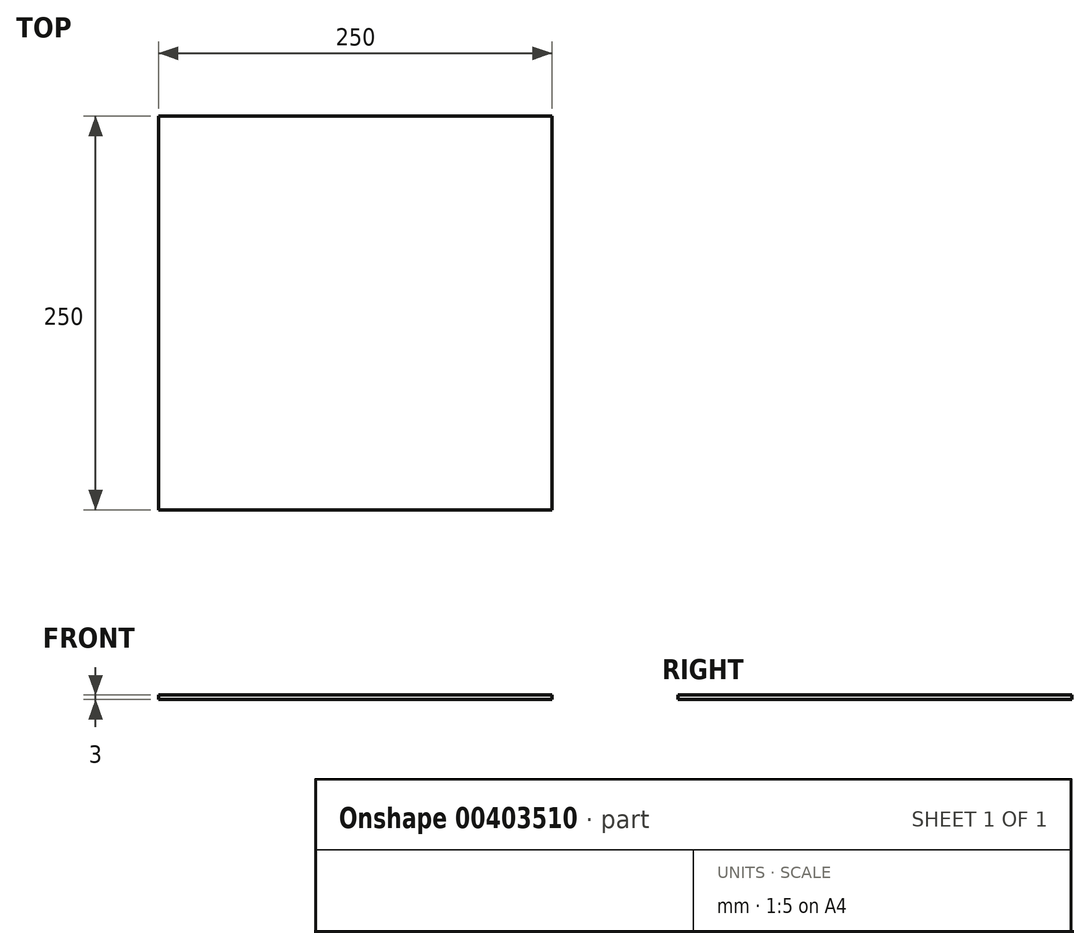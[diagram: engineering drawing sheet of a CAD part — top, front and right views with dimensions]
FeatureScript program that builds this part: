
annotation { "Feature Type Name" : "Feature", "Feature Type Description" : "" }
export const myFeature = defineFeature(function(context is Context, id is Id, definition is map)
    precondition{}
    {
        {
            var Q0;
            Q0=qCreatedBy(makeId("Top.planeOp"),FACE);
            var sketch = newSketch(context, id + "F0", { "sketchPlane" : qUnion([Q0])});
            skLineSegment(sketch, "E0.bottom", {"start": v(0, 250) * mm, "end": v(250, 250) * mm});
            skLineSegment(sketch, "E0.top", {"start": v(0, 0) * mm, "end": v(250, 0) * mm});
            skLineSegment(sketch, "E0.left", {"start": v(0, 250) * mm, "end": v(0, 0) * mm});
            skLineSegment(sketch, "E0.right", {"start": v(250, 250) * mm, "end": v(250, 0) * mm});
            skSolve(sketch);
        }
        {
            var Q0;
            Q0 = qSketchRegion(id + "F0", true);
            extrude(context, id + "F1", {"entities" : qUnion([Q0]), "depth" : 3 * mm});
        }
    });
